# Revit family: Wall_Mount-Screen-Sliding-Phantom_Screens-Motorized_Overhead_Surface_Mounted-01-CS
name_source: partatom
category: Specialty Equipment
revit_build: Autodesk Revit 2017 (Build: 20160225_1515(x64)
units: mm (PartAtom-declared; Revit-internal decimal feet)

## family parameters
Always vertical = Yes
Cut with Voids When Loaded = No
OmniClass Number = 23.30.60.21
OmniClass Title = Insect Screens
Part Type = Normal
Room Calculation Point = No
Round Connector Dimension = Use Diameter
Shared = No
Work Plane-Based = No

## types (3) — shared parameters
Assembly Code = B2010300
Description = Phantom motorized retractable screen with side tracks
Finish = Metal-Aluminum-Phantom_Screens-Classic_White
Finish Screen = Screen-Insect_Mesh-Phantom_Screens-BetterVue_Mesh
Finish Seal = Vinyl-Seal-Phantom_Screens-T-Vinyl_Black
Manufacturer = Phantom Mfg. (Int'l) Ltd.
Mesh Offset = 0' - 0 11/16"
Model = Motorized Retractable Wall Screen
Product Documentation Link = https://www.phantomscreens.com
Product Name = Motorized Overhead Wall Screens
Product Page URL = https://www.phantomscreens.com
Track Thickness = 0' - 1 17/32"
URL = https://www.phantomscreens.com

## per-type parameters (varying)
| type | 4 in Housing | 5 1/2 in Housing | 7 1/8 in Housing | Housing Height | Inside Jamb | Max Height | Max Width | Min Width | Roller Radius | Surface Mounted | Thickness | Track Height |
| 7 1/8 in Housing Surface Mount | No | No | Yes | 0' - 7 1/8" | Yes | 16' - 0" | 25' - 0" | 2' - 9" | 0' - 2 1/2" | No | 0' - 7 1/8" | 0' - 1 29/32" |
| 5 1/2 in Housing Surface Mount | No | Yes | No | 0' - 5 1/2" | Yes | 11' - 0" | 20' - 0" | 2' - 9" | 0' - 2" | No | 0' - 5 1/2" | 0' - 1 29/32" |
| 4 in Housing Surface Mount | Yes | No | No | 0' - 4" | No | 8' - 0" | 10' - 0" | 2' - 2" | 0' - 1 1/4" | Yes | 0' - 4" | 0' - 1 11/32" |

note: column(s) folded — value = type name in every type: Type Comments

## geometry (parser evidence)
native form markers: Extrusion x9, Sweep x4
no freeform markers — native parametric forms only
